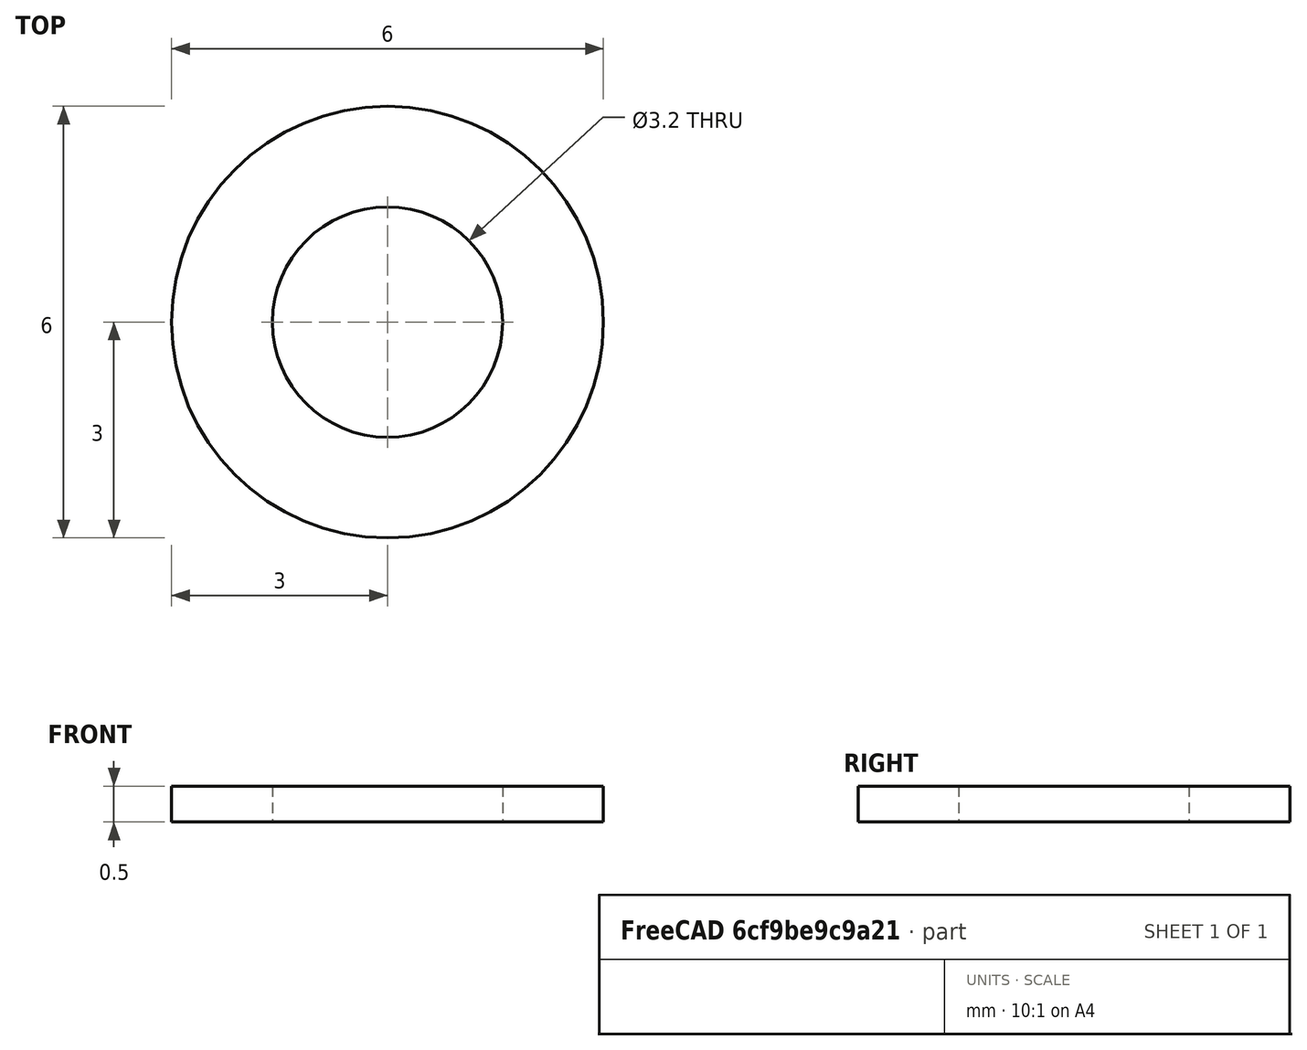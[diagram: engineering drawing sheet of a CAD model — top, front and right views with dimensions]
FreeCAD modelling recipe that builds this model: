
FCSTD DOCUMENT  (FreeCAD 0.14R3700 (Git))
Label: Scheibe DIN 433 - A 3,2
License: CC-BY 3.0
LicenseURL: http://creativecommons.org/licenses/by/3.0/
objects: Sketcher::SketchObject×1, PartDesign::Revolution×1, Part::Feature×1
note: 4 computed .brp shape members not serialized (recipe doc carries the construction recipe); baked Part::Feature solids carry a one-line shape summary decoded from their .brp

FEATURE [Sketcher::SketchObject] Sketch
  Placement = pos=(0,0,0) rot=(0.57735,0.57735,0.57735;2.0944rad)
  sketch-geometry (4):
    g0: LineSegment StartX=1.6 StartY=0 StartZ=0 EndX=3 EndY=0 EndZ=0
    g1: LineSegment StartX=3 StartY=0 StartZ=0 EndX=3 EndY=0.5 EndZ=0
    g2: LineSegment StartX=3 StartY=0.5 StartZ=0 EndX=1.6 EndY=0.5 EndZ=0
    g3: LineSegment StartX=1.6 StartY=0.5 StartZ=0 EndX=1.6 EndY=0 EndZ=0
  constraints (12):
    c: Coincident(g0,g1)
    c: Coincident(g1,g2)
    c: Coincident(g2,g3)
    c: Coincident(g3,g0)
    c: Horizontal(g0)
    c: Horizontal(g2)
    c: Vertical(g1)
    c: Vertical(g3)
    c: PointOnObject(g0,g-1)
    c: DistanceY(g1) = 0.5
    c: DistanceX(g-1,g2) = 1.6
    c: DistanceX(g-1,g1) = 3
FEATURE [PartDesign::Revolution] Revolution  label="Scheibe DIN 433 - A 3,2 #"
  Angle = 360
  Axis = (0,0,1)
  Base = (0,0,0)
  Placement = pos=(0,0,0) rot=(0.57735,0.57735,0.57735;2.0944rad)
  ReferenceAxis = -> Sketch [V_Axis]
  Reversed = true
  Sketch = -> Sketch
FEATURE [Part::Feature] Revolution001  label="Scheibe DIN 433 - A 3,2 #001"
  Placement = pos=(0,0,0) rot=(0.57735,0.57735,0.57735;2.0944rad)
  shape: bbox 6 x 6 x 0.5 mm, 4 faces (baked)
